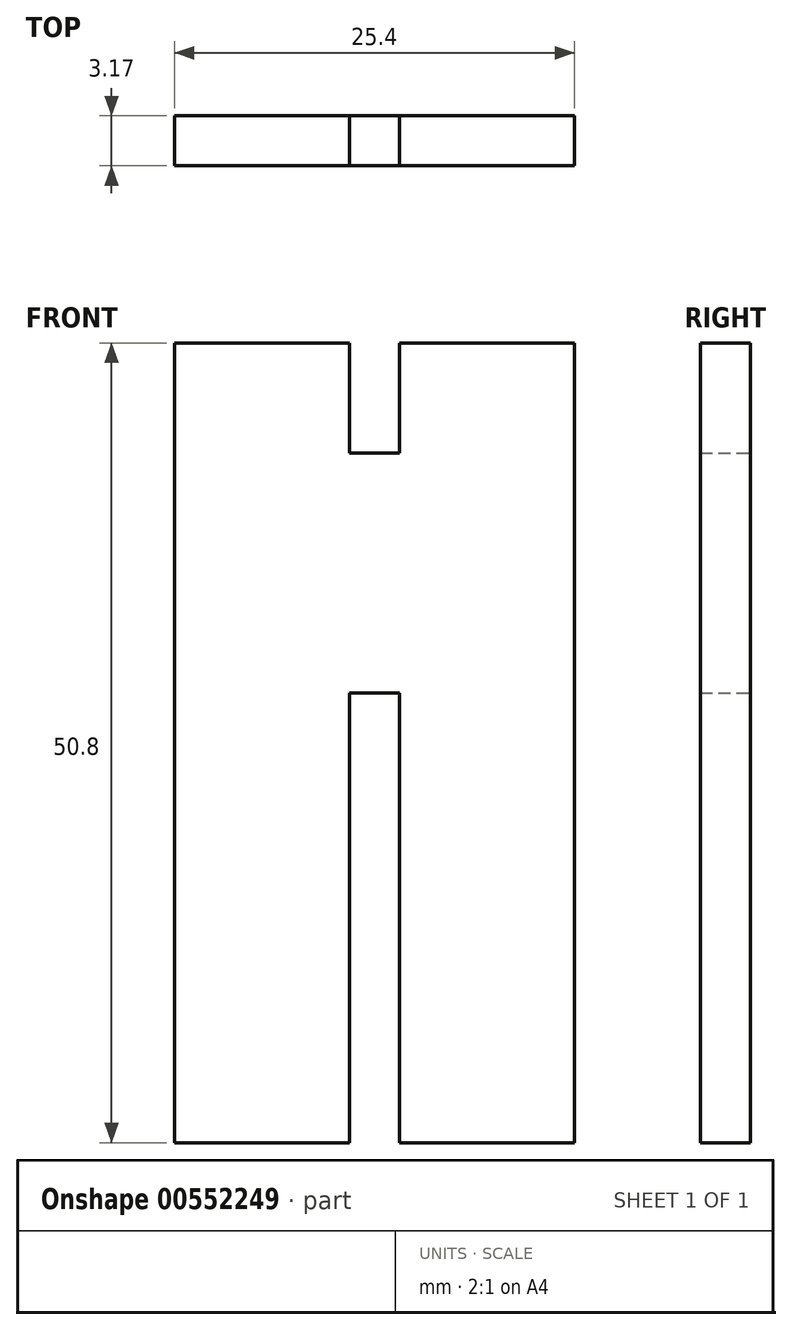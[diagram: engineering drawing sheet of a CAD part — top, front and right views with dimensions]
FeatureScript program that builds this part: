
annotation { "Feature Type Name" : "Feature", "Feature Type Description" : "" }
export const myFeature = defineFeature(function(context is Context, id is Id, definition is map)
    precondition{}
    {
        {
            var Q0;
            Q0=qCreatedBy(makeId("Front.planeOp"),FACE);
            var sketch = newSketch(context, id + "F0", { "sketchPlane" : qUnion([Q0])});
            skLineSegment(sketch, "E0.left", {"start": v(12.7, 25.4) * mm, "end": v(12.7, -25.4) * mm});
            skLineSegment(sketch, "E0.right", {"start": v(-12.7, 25.4) * mm, "end": v(-12.7, -25.4) * mm});
            skPoint(sketch, "E0.middle", {"position": v(0, 0) * mm});
            skLineSegment(sketch, "E1", {"start": v(3.17, 25.4) * mm, "end": v(12.7, 25.4) * mm});
            skLineSegment(sketch, "E2", {"start": v(-3.18, 25.4) * mm, "end": v(-12.7, 25.4) * mm});
            skLineSegment(sketch, "E3", {"start": v(-12.7, -25.4) * mm, "end": v(-3.18, -25.4) * mm});
            skLineSegment(sketch, "E4", {"start": v(12.7, -25.4) * mm, "end": v(3.17, -25.4) * mm});
            skLineSegment(sketch, "E5", {"start": v(3.17, 25.4) * mm, "end": v(1.59, 25.4) * mm});
            skLineSegment(sketch, "E6", {"start": v(-3.18, 25.4) * mm, "end": v(-1.59, 25.4) * mm});
            skLineSegment(sketch, "E7", {"start": v(1.59, 25.4) * mm, "end": v(1.59, 18.41) * mm});
            skLineSegment(sketch, "E8", {"start": v(1.59, 18.41) * mm, "end": v(-1.59, 18.41) * mm});
            skLineSegment(sketch, "E9", {"start": v(-1.59, 25.4) * mm, "end": v(-1.59, 18.41) * mm});
            skLineSegment(sketch, "E10", {"start": v(-3.18, -25.4) * mm, "end": v(-1.59, -25.4) * mm});
            skLineSegment(sketch, "E11", {"start": v(-1.59, -25.4) * mm, "end": v(-1.59, 3.18) * mm});
            skLineSegment(sketch, "E12", {"start": v(-1.59, 3.18) * mm, "end": v(0, 3.18) * mm});
            skLineSegment(sketch, "E13", {"start": v(3.17, -25.4) * mm, "end": v(1.59, -25.4) * mm});
            skLineSegment(sketch, "E14", {"start": v(1.59, -25.4) * mm, "end": v(1.59, 3.18) * mm});
            skLineSegment(sketch, "E15", {"start": v(0, 3.18) * mm, "end": v(1.59, 3.18) * mm});
            skSolve(sketch);
        }
        {
            var Q0;
            Q0=makeQuery(id+"F0.imprint","IMPRINT",FACE,{"disambiguationData":[TD([[makeQuery(id+"F0.imprint","IMPRINT",EDGE,{"derivedFrom":sQuery(id+"F0.wireOp",EDGE,"E0.left")}),-1.0]])]});
            extrude(context, id + "F1", {"entities" : qUnion([Q0]), "depth" : 3.17 * mm, "offsetDistance" : 25.4 * mm});
        }
    });
